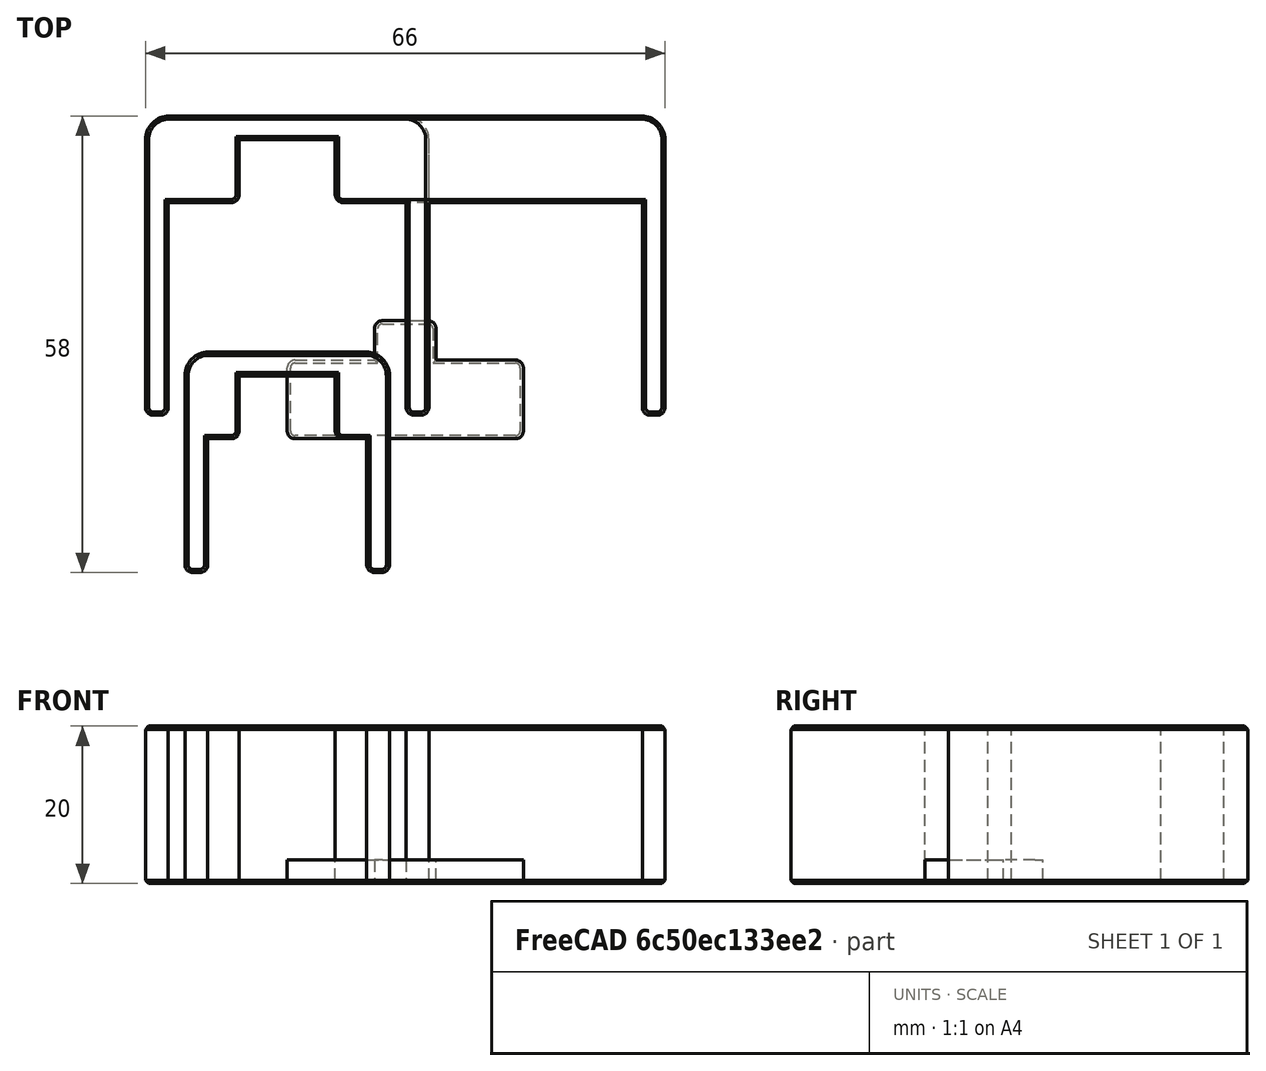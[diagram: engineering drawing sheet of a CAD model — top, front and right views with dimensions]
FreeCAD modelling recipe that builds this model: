
FCSTD DOCUMENT  (FreeCAD 0.19R24291 (Git))
Label: rail-aligner-wider
License: Other
LicenseURL: GPL3
objects: Part::Box×12, Part::Fillet×10, Part::Chamfer×5, Part::MultiFuse×4, Part::Cut×4
note: 35 computed .brp shape members not serialized (recipe doc carries the construction recipe); baked Part::Feature solids carry a one-line shape summary decoded from their .brp

FEATURE [Part::Box] Box  label="Cube"
  AttacherType = Attacher::AttachEngine3D
  Height = 4
  Length = 30
  Width = 10
FEATURE [Part::Box] Box001  label="Cube001"
  AttacherType = Attacher::AttachEngine3D
  Height = 4
  Length = 7.8
  Placement = pos=(11.1,5,0) rot=(0,0,1;0rad)
  Width = 10
FEATURE [Part::Fillet] Fillet
  Base = -> Box
  Edges = 4 edges r=1: [Edge1,Edge3,Edge5,Edge7]
FEATURE [Part::Fillet] Fillet001
  Base = -> Box001
  Edges = 2 edges r=1: [Edge3,Edge7]
FEATURE [Part::Chamfer] Chamfer
  Base = -> Fillet
  Edges = 8 edges r=0.4: [Edge3,Edge12,Edge14,Edge16,Edge17,Edge18,Edge19,Edge20]
FEATURE [Part::Chamfer] Chamfer001
  Base = -> Fillet001
  Edges = 6 edges r=0.4: [Edge3,Edge10,Edge12,Edge14,Edge15,Edge16]
FEATURE [Part::MultiFuse] Fusion
  Shapes = -> [Chamfer,Chamfer001]
FEATURE [Part::Box] Box002  label="Cube002"
  AttacherType = Attacher::AttachEngine3D
  Height = 10
  Length = 30
  Placement = pos=(0,0,3) rot=(0,0,1;0rad)
  Width = 15
FEATURE [Part::Cut] Cut
  Base = -> Fusion
  Tool = -> Box002
FEATURE [Part::Box] Box003  label="Cube003"
  AttacherType = Attacher::AttachEngine3D
  Height = 20
  Length = 36
  Placement = pos=(-18,3,0) rot=(0,0,1;0rad)
  Width = 38
FEATURE [Part::Box] Box004  label="Cube004"
  AttacherType = Attacher::AttachEngine3D
  Height = 20
  Length = 30.2
  Placement = pos=(-15.1,0,0) rot=(0,0,1;0rad)
  Width = 30
FEATURE [Part::Box] Box005  label="Cube005"
  AttacherType = Attacher::AttachEngine3D
  Height = 20
  Length = 12.2
  Placement = pos=(-6.1,30,0) rot=(0,0,1;0rad)
  Width = 8
FEATURE [Part::Fillet] Fillet002
  Base = -> Box003
  Edges = 2 edges r=3: [Edge3,Edge7]
FEATURE [Part::Fillet] Fillet003  label="30-base"
  Base = -> Fillet002
  Edges = 2 edges r=1: [Edge2,Edge13]
FEATURE [Part::Box] Box006  label="Cube006"
  AttacherType = Attacher::AttachEngine3D
  Height = 20
  Length = 66
  Placement = pos=(-18,3,0) rot=(0,0,1;0rad)
  Width = 38
FEATURE [Part::Fillet] Fillet004
  Base = -> Box006
  Edges = 2 edges r=3: [Edge3,Edge7]
FEATURE [Part::Fillet] Fillet005  label="60-base"
  Base = -> Fillet004
  Edges = 2 edges r=1: [Edge2,Edge13]
FEATURE [Part::Box] Box007  label="Cube007"
  AttacherType = Attacher::AttachEngine3D
  Height = 20
  Length = 60.2
  Placement = pos=(-15.1,0,0) rot=(0,0,1;0rad)
  Width = 30
FEATURE [Part::Box] Box008  label="Cube008"
  AttacherType = Attacher::AttachEngine3D
  Height = 20
  Length = 12.2
  Placement = pos=(-6.1,30,0) rot=(0,0,1;0rad)
  Width = 8
FEATURE [Part::Box] Box009  label="Cube009"
  AttacherType = Attacher::AttachEngine3D
  Height = 20
  Length = 12.2
  Placement = pos=(-6.1,0,0) rot=(0,0,1;0rad)
  Width = 8
FEATURE [Part::Box] Box010  label="Cube010"
  AttacherType = Attacher::AttachEngine3D
  Height = 20
  Length = 20.2
  Placement = pos=(-10.1,-20,0) rot=(0,0,1;0rad)
  Width = 20
FEATURE [Part::Box] Box011  label="Cube011"
  AttacherType = Attacher::AttachEngine3D
  Height = 20
  Length = 26
  Placement = pos=(-13,-17,0) rot=(0,0,1;0rad)
  Width = 28
FEATURE [Part::MultiFuse] Fusion003
  Shapes = -> [Box010,Box009]
FEATURE [Part::Cut] Cut003
  Base = -> Box011
  Tool = -> Fusion003
FEATURE [Part::Fillet] Fillet008
  Base = -> Cut003
  Edges = 6 edges r=1: [Edge1,Edge6,Edge30,Edge31,Edge33,Edge36]
FEATURE [Part::Fillet] Fillet009
  Base = -> Fillet008
  Edges = 2 edges r=3: [Edge4,Edge25]
FEATURE [Part::Chamfer] Chamfer004  label="20-aligner"
  Base = -> Fillet009
  Edges = 40 edges r=0.4: [Edge1,Edge3,Edge5,Edge6,Edge7,Edge8,Edge9,Edge10,Edge11,Edge12,Edge13,Edge14,Edge15,Edge16,Edge17,Edge18,Edge19,Edge20,Edge21,Edge22,Edge23,Edge24,Edge26,Edge28,Edge29,Edge30,Edge31,Edge32,Edge33,Edge34,Edge35,Edge36,Edge37,Edge38,Edge39,Edge40,Edge41,Edge42,Edge43,Edge44]
FEATURE [Part::MultiFuse] Fusion004
  Shapes = -> [Box005,Box004]
FEATURE [Part::Cut] Cut004
  Base = -> Fillet003
  Tool = -> Fusion004
FEATURE [Part::Fillet] Fillet010
  Base = -> Cut004
  Edges = 4 edges r=1: [Edge41,Edge43,Edge46,Edge48]
FEATURE [Part::Chamfer] Chamfer005  label="30-aligner"
  Base = -> Fillet010
  Edges = 40 edges r=0.4: [Edge1,Edge2,Edge3,Edge4,Edge5,Edge6,Edge7,Edge8,Edge9,Edge10,Edge11,Edge12,Edge13,Edge14,Edge15,Edge16,Edge17,Edge18,Edge19,Edge20,Edge21,Edge25,Edge26,Edge28,Edge30,Edge32,Edge34,Edge36,Edge38,Edge40,Edge42,Edge44,Edge47,Edge49,Edge50,Edge52,Edge54,Edge56,Edge58,Edge60]
FEATURE [Part::MultiFuse] Fusion005
  Shapes = -> [Box008,Box007]
FEATURE [Part::Cut] Cut005
  Base = -> Fillet005
  Tool = -> Fusion005
FEATURE [Part::Fillet] Fillet011
  Base = -> Cut005
  Edges = 4 edges r=1: [Edge41,Edge43,Edge46,Edge48]
FEATURE [Part::Chamfer] Chamfer006  label="60-aligner"
  Base = -> Fillet011
  Edges = 40 edges r=0.4: [Edge1,Edge2,Edge3,Edge4,Edge5,Edge6,Edge7,Edge8,Edge9,Edge10,Edge11,Edge12,Edge13,Edge14,Edge15,Edge16,Edge17,Edge18,Edge19,Edge20,Edge21,Edge25,Edge26,Edge28,Edge30,Edge32,Edge34,Edge36,Edge38,Edge40,Edge42,Edge44,Edge47,Edge49,Edge50,Edge52,Edge54,Edge56,Edge58,Edge60]
